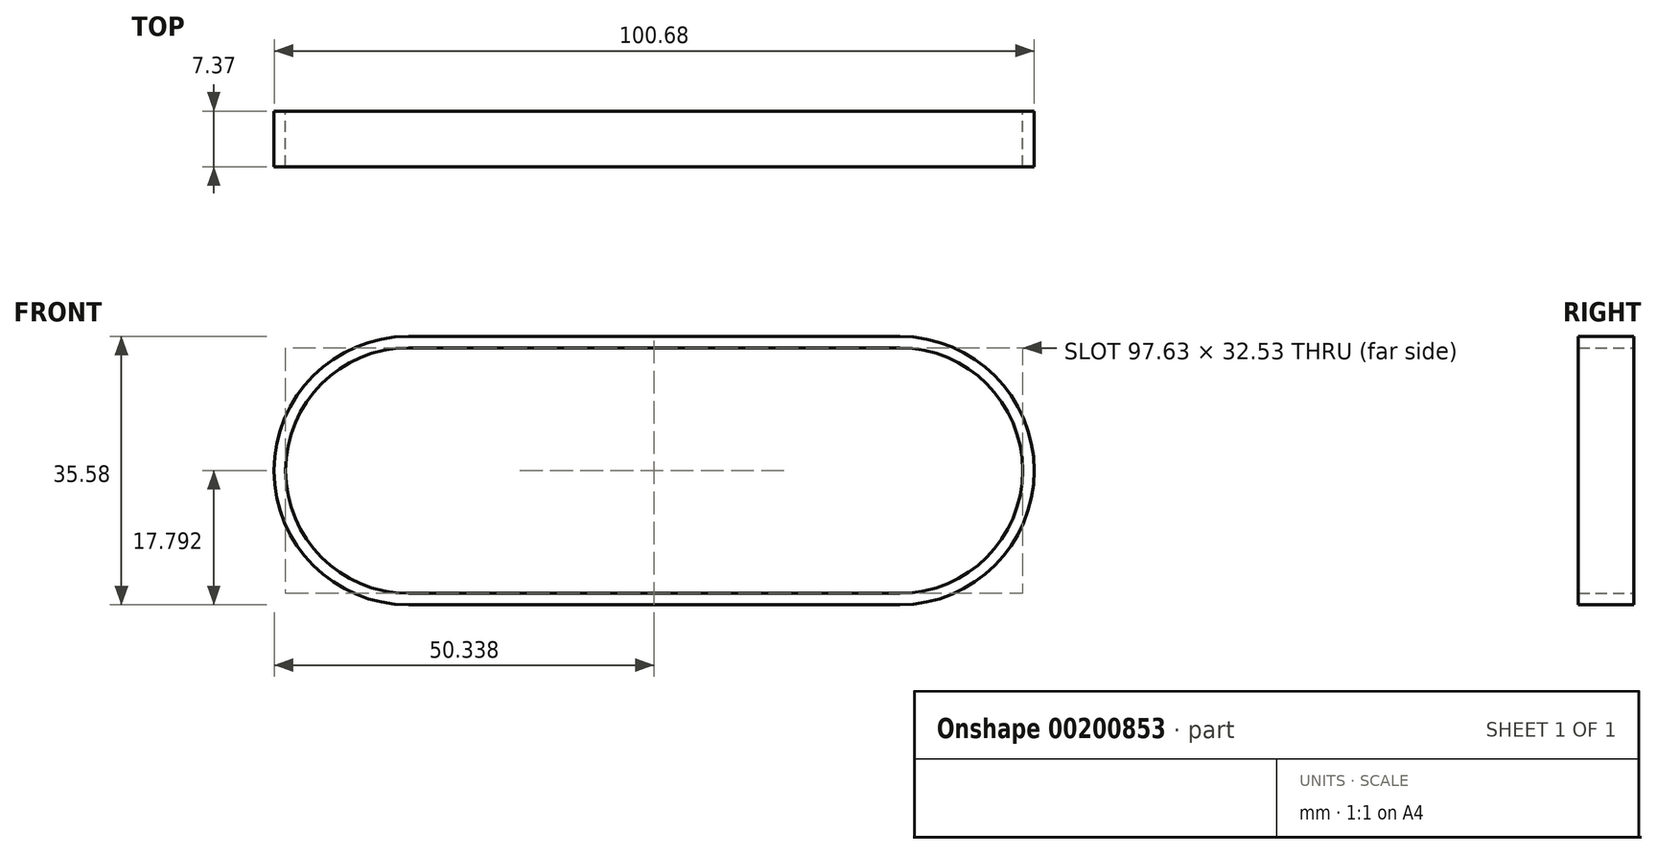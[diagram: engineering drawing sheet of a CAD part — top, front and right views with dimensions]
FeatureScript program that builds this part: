
annotation { "Feature Type Name" : "Feature", "Feature Type Description" : "" }
export const myFeature = defineFeature(function(context is Context, id is Id, definition is map)
    precondition{}
    {
        {
            var Q0;
            Q0=qCreatedBy(makeId("Front.planeOp"),FACE);
            var sketch = newSketch(context, id + "F0", { "sketchPlane" : qUnion([Q0])});
            skLineSegment(sketch, "E0.bottom", {"start": v(-58.93, 42.1) * mm, "end": v(6.18, 42.1) * mm});
            skLineSegment(sketch, "E0.top", {"start": v(-58.93, 6.52) * mm, "end": v(6.18, 6.52) * mm});
            skArc(sketch, "E1", {"start": v(-58.93, 6.52) * mm, "mid": v(-76.71, 24.31) * mm, "end": v(-58.93, 42.1) * mm});
            skArc(sketch, "E2", {"start": v(6.18, 42.1) * mm, "mid": v(23.97, 24.31) * mm, "end": v(6.18, 6.52) * mm});
            skLineSegment(sketch, "E3.0", {"start": v(-58.93, 40.58) * mm, "end": v(6.18, 40.58) * mm});
            skArc(sketch, "E3.1", {"start": v(-58.93, 8.05) * mm, "mid": v(-75.19, 24.31) * mm, "end": v(-58.93, 40.58) * mm});
            skLineSegment(sketch, "E3.2", {"start": v(-58.93, 8.05) * mm, "end": v(6.18, 8.05) * mm});
            skArc(sketch, "E3.3", {"start": v(6.18, 40.58) * mm, "mid": v(22.44, 24.31) * mm, "end": v(6.18, 8.05) * mm});
            skSolve(sketch);
        }
        {
            var Q0;
            Q0 = qSketchRegion(id + "F0", true);
            extrude(context, id + "F1", {"entities" : qUnion([Q0]), "depth" : 7.37 * mm});
        }
    });
